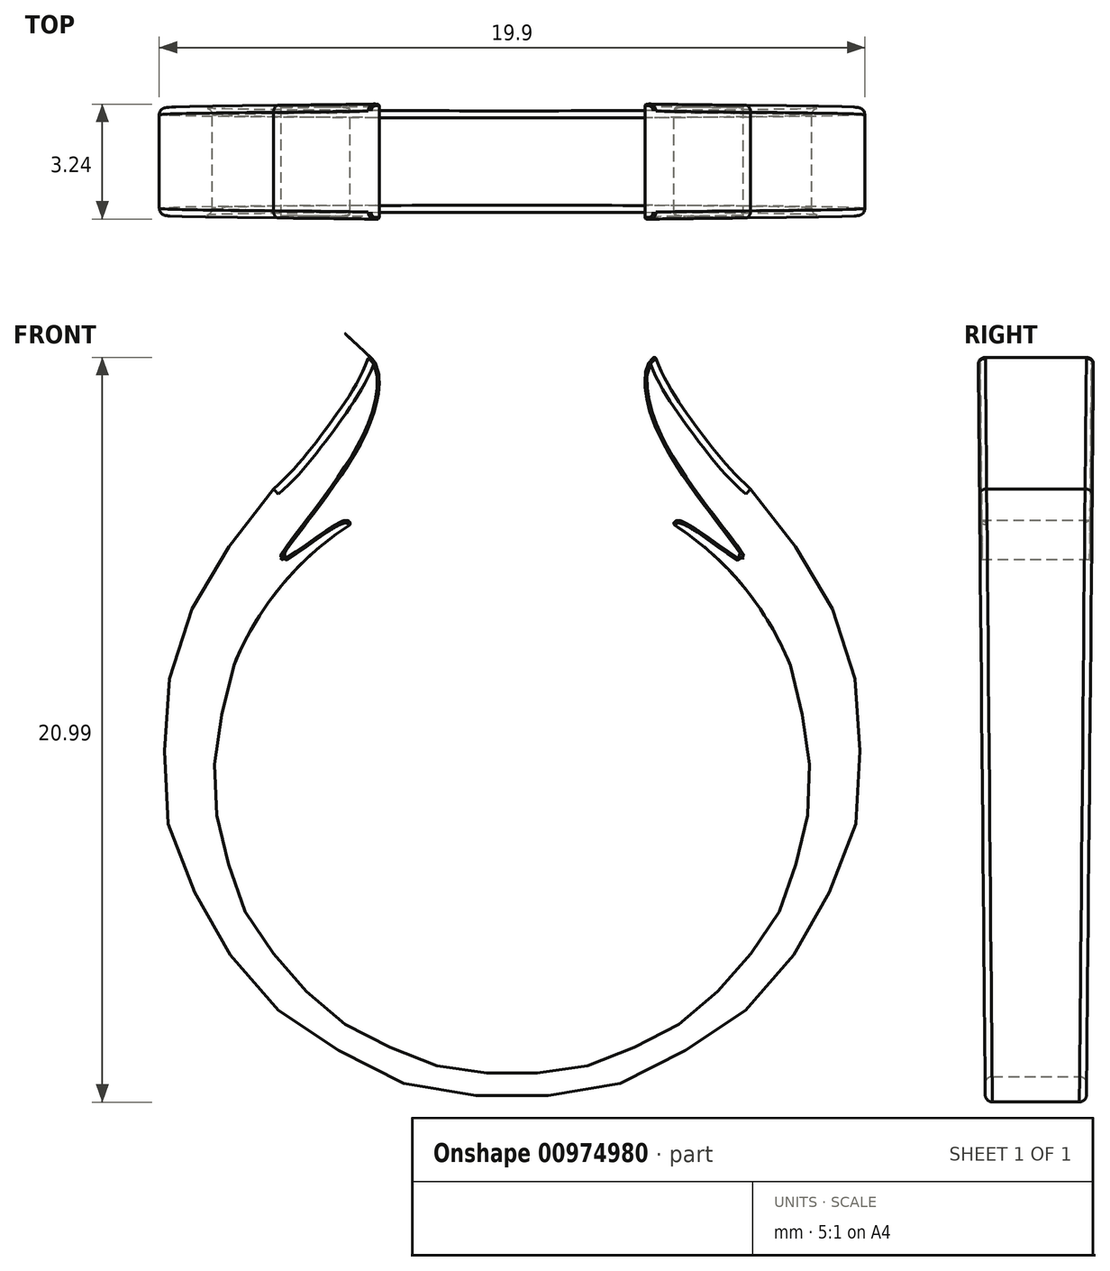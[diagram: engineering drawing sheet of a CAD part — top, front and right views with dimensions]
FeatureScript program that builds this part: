
annotation { "Feature Type Name" : "Feature", "Feature Type Description" : "" }
export const myFeature = defineFeature(function(context is Context, id is Id, definition is map)
    precondition{}
    {
        {
            var Q0;
            Q0=qCreatedBy(makeId("Front.planeOp"),FACE);
            var sketch = newSketch(context, id + "F0", { "sketchPlane" : qUnion([Q0])});
            skArc(sketch, "E0", {"start": v(-6.73, 8.12) * mm, "mid": v(0, -9.16) * mm, "end": v(6.73, 8.12) * mm});
            skArc(sketch, "E1", {"start": v(-4.55, 7.12) * mm, "mid": v(0, -8.45) * mm, "end": v(4.55, 7.12) * mm});
            skFitSpline(sketch, "E2", {"points": [v(-6.73, 8.12) * mm, v(-5.1, 10.01) * mm, v(-4.03, 11.86) * mm], "startDerivative": vector(3.3, 2.81) * mm, "endDerivative": vector(1.57, 4.42) * mm});
            skFitSpline(sketch, "E3", {"points": [v(-4.03, 11.86) * mm, v(-3.8, 11.54) * mm, v(-4.3, 9.33) * mm, v(-6.5, 6.11) * mm, v(-4.96, 7.12) * mm, v(-4.55, 7.12) * mm], "startDerivative": vector(2.68, -2.55) * mm, "endDerivative": vector(1.26, -4.37) * mm});
            skFitSpline(sketch, "E4.MirrorCS", {"points": [v(6.73, 8.12) * mm, v(5.1, 10.01) * mm, v(4.03, 11.86) * mm], "startDerivative": vector(-3.3, 2.81) * mm, "endDerivative": vector(-1.57, 4.42) * mm});
            skFitSpline(sketch, "E5.MirrorCS", {"points": [v(4.03, 11.86) * mm, v(3.8, 11.54) * mm, v(4.3, 9.33) * mm, v(6.5, 6.11) * mm, v(4.96, 7.12) * mm, v(4.55, 7.12) * mm], "startDerivative": vector(-2.68, -2.55) * mm, "endDerivative": vector(-1.26, -4.37) * mm});
            skSolve(sketch);
        }
        {
            var Q0;
            Q0 = qSketchRegion(id + "F0", true);
            extrude(context, id + "F1", {"entities" : qUnion([Q0]), "endBound" : BoundingType.SYMMETRIC, "depth" : 3.25 * mm, "offsetDistance" : 25 * mm});
        }
        {
            var Q0;
            Q0=qCreatedBy(makeId("Right.planeOp"),FACE);
            var sketch = newSketch(context, id + "F2", { "sketchPlane" : qUnion([Q0])});
            skLineSegment(sketch, "E6", {"start": v(-1.64, 13.94) * mm, "end": v(-1.4, -12.17) * mm});
            skLineSegment(sketch, "E7", {"start": v(-1.4, -12.16) * mm, "end": v(-6.23, -12.16) * mm});
            skLineSegment(sketch, "E8", {"start": v(-6.23, -12.17) * mm, "end": v(-1.64, 13.94) * mm});
            skLineSegment(sketch, "E9.MirrorCS", {"start": v(1.64, 13.94) * mm, "end": v(1.4, -12.17) * mm});
            skLineSegment(sketch, "E10.MirrorCS", {"start": v(1.4, -12.16) * mm, "end": v(6.23, -12.16) * mm});
            skLineSegment(sketch, "E11.MirrorCS", {"start": v(6.23, -12.17) * mm, "end": v(1.64, 13.94) * mm});
            skSolve(sketch);
        }
        {
            var Q0;
            Q0 = qSketchRegion(id + "F2", true);
            extrude(context, id + "F3", {"entities" : qUnion([Q0]), "operationType" : NewBodyOperationType.REMOVE, "endBound" : BoundingType.SYMMETRIC, "oppositeDirection" : true, "depth" : 25 * mm, "offsetDistance" : 25 * mm});
        }
        {
            var Q0;
            Q0=makeQuery(id+"F3.boolean.opBoolean","INTERSECT",EDGE,{"derivedFrom":[makeQuery(id+"F1.opExtrude","SWEPT_FACE",FACE,{"disambiguationData":[OSD([sQuery(id+"F0.wireOp",EDGE,"E1")])]}),makeQuery(id+"F3.opExtrude","SWEPT_FACE",FACE,{"disambiguationData":[OSD([sQuery(id+"F2.wireOp",EDGE,"E6")])]})]});
            var Q1;
            Q1=makeQuery(id+"F3.boolean.opBoolean","INTERSECT",EDGE,{"derivedFrom":[makeQuery(id+"F1.opExtrude","SWEPT_FACE",FACE,{"disambiguationData":[OSD([sQuery(id+"F0.wireOp",EDGE,"E1")])]}),makeQuery(id+"F3.opExtrude","SWEPT_FACE",FACE,{"disambiguationData":[OSD([sQuery(id+"F2.wireOp",EDGE,"E9.MirrorCS")])]})]});
            var Q2;
            Q2=makeQuery(id+"F3.boolean.opBoolean","INTERSECT",EDGE,{"derivedFrom":[makeQuery(id+"F1.opExtrude","SWEPT_FACE",FACE,{"disambiguationData":[OSD([sQuery(id+"F0.wireOp",EDGE,"E0")])]}),makeQuery(id+"F3.opExtrude","SWEPT_FACE",FACE,{"disambiguationData":[OSD([sQuery(id+"F2.wireOp",EDGE,"E6")])]})]});
            var Q3;
            Q3=makeQuery(id+"F3.boolean.opBoolean","INTERSECT",EDGE,{"derivedFrom":[makeQuery(id+"F1.opExtrude","SWEPT_FACE",FACE,{"disambiguationData":[OSD([sQuery(id+"F0.wireOp",EDGE,"E0")])]}),makeQuery(id+"F3.opExtrude","SWEPT_FACE",FACE,{"disambiguationData":[OSD([sQuery(id+"F2.wireOp",EDGE,"E9.MirrorCS")])]})]});
            fillet(context, id + "F4", {"entities" : qUnion([Q0, Q1, Q2, Q3]), "radius" : 0.2 * mm, "tangentPropagation" : true, "allowEdgeOverflow" : false});
        }
        {
            var Q0;
            Q0=makeQuery(id+"F1.opExtrude","SWEPT_EDGE",EDGE,{"disambiguationData":[OSD([sQuery(id+"F0.wireOp",EDGE,"E1"),sQuery(id+"F0.wireOp",EDGE,"E5.MirrorCS")])]});
            var Q1;
            Q1=makeQuery(id+"F1.opExtrude","SWEPT_EDGE",EDGE,{"disambiguationData":[OSD([sQuery(id+"F0.wireOp",EDGE,"E1"),sQuery(id+"F0.wireOp",EDGE,"E3")])]});
            fillet(context, id + "F5", {"entities" : qUnion([Q0, Q1]), "radius" : 0.05 * mm, "tangentPropagation" : true, "allowEdgeOverflow" : false});
        }
    });
